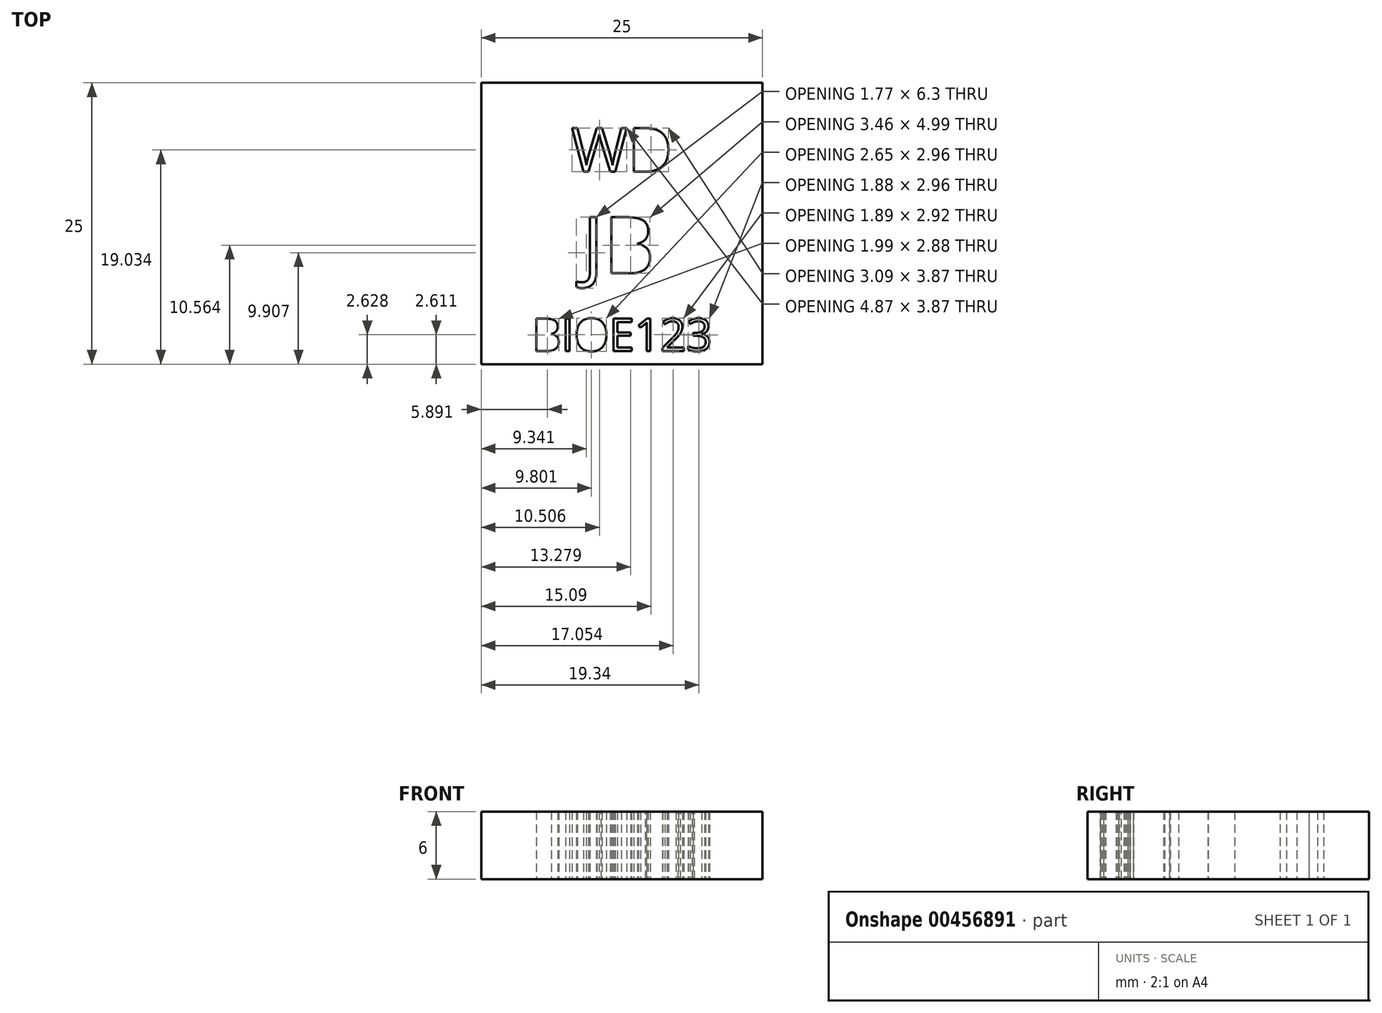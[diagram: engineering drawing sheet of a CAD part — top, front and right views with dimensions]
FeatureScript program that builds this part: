
annotation { "Feature Type Name" : "Feature", "Feature Type Description" : "" }
export const myFeature = defineFeature(function(context is Context, id is Id, definition is map)
    precondition{}
    {
        {
            var Q0;
            Q0=qCreatedBy(makeId("Top.planeOp"),FACE);
            var sketch = newSketch(context, id + "F0", { "sketchPlane" : qUnion([Q0])});
            skPoint(sketch, "E0.middle", {"position": v(0, 0) * mm});
            skLineSegment(sketch, "E1.bottom", {"start": v(12.5, 12.5) * mm, "end": v(-12.5, 12.5) * mm});
            skLineSegment(sketch, "E1.top", {"start": v(12.5, -12.5) * mm, "end": v(-12.5, -12.5) * mm});
            skLineSegment(sketch, "E1.left", {"start": v(12.5, 12.5) * mm, "end": v(12.5, -12.5) * mm});
            skLineSegment(sketch, "E1.right", {"start": v(-12.5, 12.5) * mm, "end": v(-12.5, -12.5) * mm});
            skText(sketch, "E2", { "text": "WD", "fontName": "OpenSans-Regular.ttf"});
            skText(sketch, "E3", { "text": "JB", "fontName": "OpenSans-Regular.ttf"});
            skText(sketch, "E4", { "text": "BIOE123", "fontName": "OpenSans-Regular.ttf"});
            const initialGuessF0  = {"E2": [-0.0045, 0.0046, 1, 0, 0.0039], "E3": [-0.0035, -0.00443, 1, 0, 0.00503], "E4": [-0.008, -0.01133, 1, 0, 0.0029]};
            skSetInitialGuess(sketch, initialGuessF0);
            skSolve(sketch);
        }
        {
            var Q0;
            Q0 = qSketchRegion(id + "F0", true);
            extrude(context, id + "F1", {"entities" : qUnion([Q0]), "depth" : 6 * mm});
        }
    });
